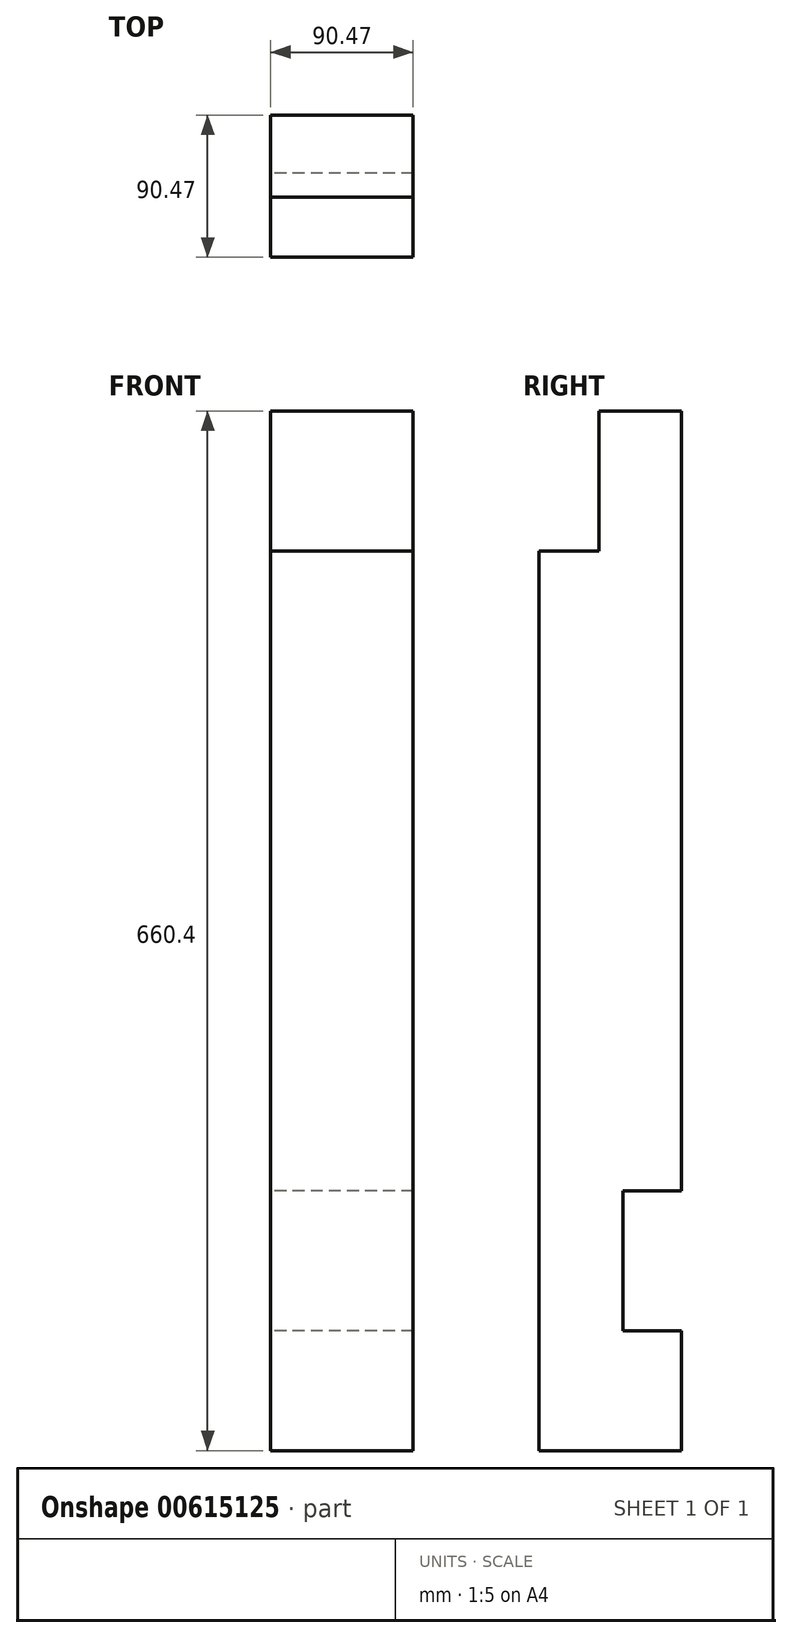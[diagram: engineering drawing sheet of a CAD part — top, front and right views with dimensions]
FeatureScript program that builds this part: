
annotation { "Feature Type Name" : "Feature", "Feature Type Description" : "" }
export const myFeature = defineFeature(function(context is Context, id is Id, definition is map)
    precondition{}
    {
        {
            var Q0;
            Q0=qCreatedBy(makeId("Right.planeOp"),FACE);
            var sketch = newSketch(context, id + "F0", { "sketchPlane" : qUnion([Q0])});
            skLineSegment(sketch, "E0.right", {"start": v(-61.33, 407.2) * mm, "end": v(-61.33, -253.2) * mm});
            skLineSegment(sketch, "E1.right", {"start": v(-62.35, -88.1) * mm, "end": v(-62.35, -177) * mm});
            skLineSegment(sketch, "E2.MirrorCS", {"start": v(-98.41, -177) * mm, "end": v(-60.31, -177) * mm});
            skLineSegment(sketch, "E3.MirrorCS", {"start": v(-98.41, -88.1) * mm, "end": v(-60.31, -88.1) * mm});
            skLineSegment(sketch, "E4.MirrorCS", {"start": v(-113.7, 407.2) * mm, "end": v(-113.7, 318.3) * mm});
            skLineSegment(sketch, "E5.MirrorCS", {"start": v(-151.8, 407.2) * mm, "end": v(-151.8, 318.3) * mm});
            skLineSegment(sketch, "E6.MirrorCS", {"start": v(-151.8, 318.3) * mm, "end": v(-113.7, 318.3) * mm});
            skLineSegment(sketch, "E7.MirrorCS", {"start": v(-151.8, 407.2) * mm, "end": v(-113.7, 407.2) * mm});
            skLineSegment(sketch, "E8.MirrorCS", {"start": v(-151.8, 407.2) * mm, "end": v(-151.8, -253.2) * mm});
            skLineSegment(sketch, "E9.MirrorCS", {"start": v(-151.8, -253.2) * mm, "end": v(-61.33, -253.2) * mm});
            skLineSegment(sketch, "E10.MirrorCS", {"start": v(-151.8, 407.2) * mm, "end": v(-61.33, 407.2) * mm});
            skLineSegment(sketch, "E11.MirrorCS", {"start": v(-98.41, -88.1) * mm, "end": v(-98.41, -177) * mm});
            skSolve(sketch);
        }
        {
            var Q0;
            {var subQ7=sQuery(id+"F0.wireOp",EDGE,"E9.MirrorCS");Q0=makeQuery(id+"F0.imprint","IMPRINT",FACE,{"disambiguationData":[TD([[makeQuery(id+"F0.imprint","IMPRINT",EDGE,{"derivedFrom":subQ7}),1.0]])]});}
            extrude(context, id + "F1", {"entities" : qUnion([Q0]), "depth" : 90.47 * mm});
        }
    });
